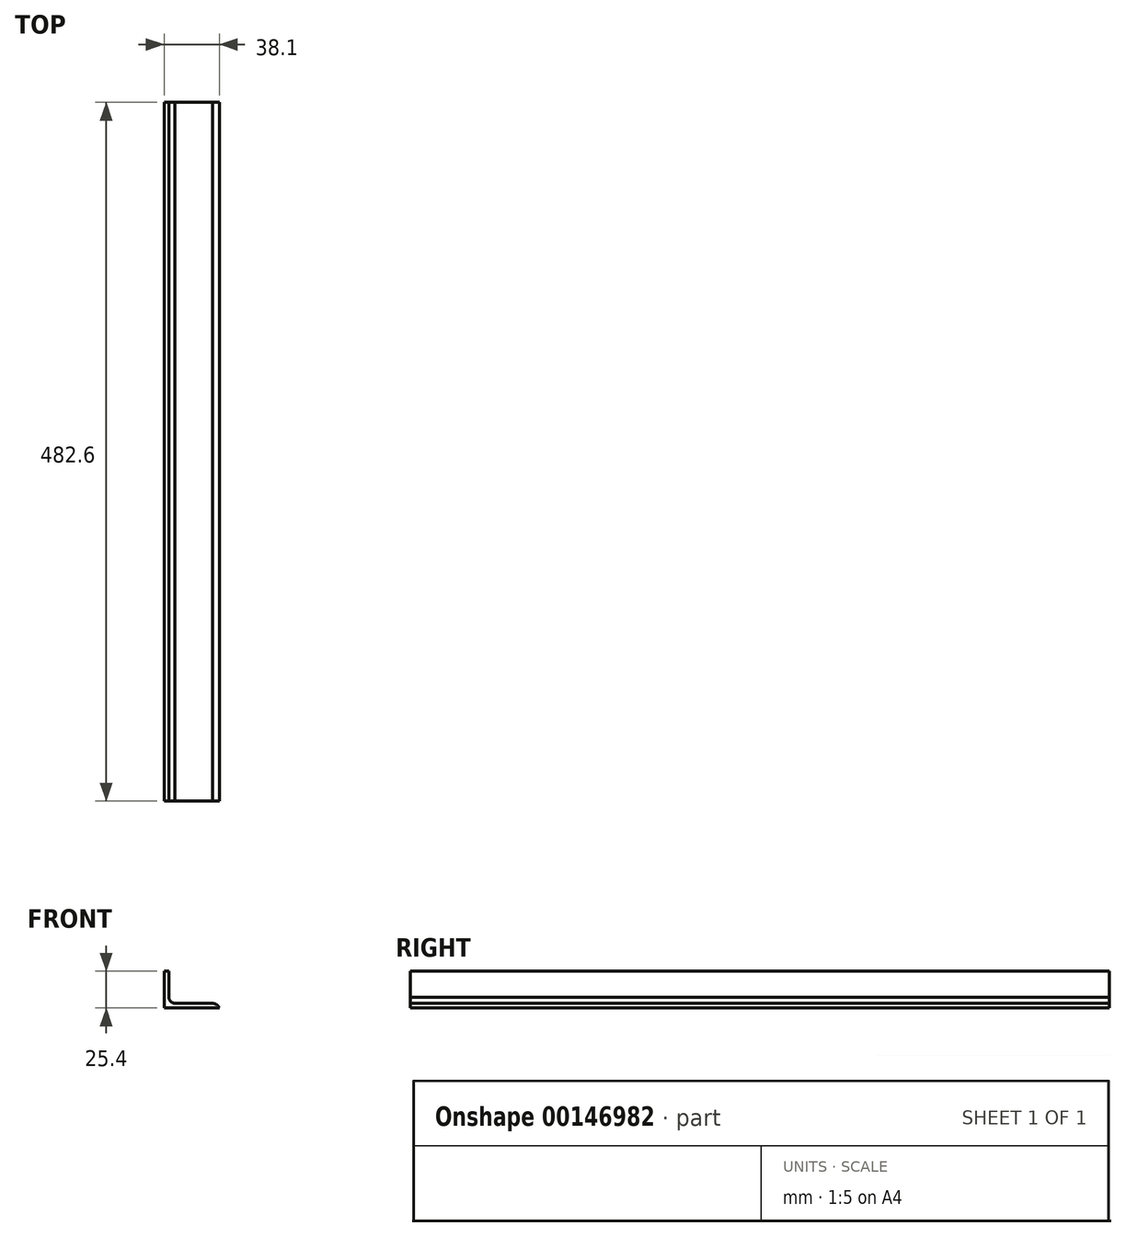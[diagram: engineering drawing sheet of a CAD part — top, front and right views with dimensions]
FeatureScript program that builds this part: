
annotation { "Feature Type Name" : "Feature", "Feature Type Description" : "" }
export const myFeature = defineFeature(function(context is Context, id is Id, definition is map)
    precondition{}
    {
        {
            var Q0;
            Q0=qCreatedBy(makeId("Front.planeOp"),FACE);
            var sketch = newSketch(context, id + "F0", { "sketchPlane" : qUnion([Q0])});
            skLineSegment(sketch, "E0.bottom", {"start": v(0, 0) * mm, "end": v(3.17, 0) * mm});
            skLineSegment(sketch, "E0.left", {"start": v(0, 0) * mm, "end": v(0, 25.4) * mm});
            skLineSegment(sketch, "E0.right", {"start": v(3.17, 7.3) * mm, "end": v(3.17, 25.4) * mm});
            skLineSegment(sketch, "E1.bottom", {"start": v(0, 0) * mm, "end": v(38.1, 0) * mm});
            skLineSegment(sketch, "E1.top", {"start": v(7.5, 3.17) * mm, "end": v(33.34, 3.17) * mm});
            skLineSegment(sketch, "E1.left", {"start": v(0, 0) * mm, "end": v(0, 3.17) * mm});
            skArc(sketch, "E2", {"start": v(38.1, 0) * mm, "mid": v(36.24, 2.37) * mm, "end": v(33.34, 3.17) * mm});
            skArc(sketch, "E3", {"start": v(3.17, 7.3) * mm, "mid": v(4.62, 4.5) * mm, "end": v(7.5, 3.17) * mm});
            skLineSegment(sketch, "E4", {"start": v(0, 25.4) * mm, "end": v(3.17, 25.4) * mm});
            skSolve(sketch);
        }
        {
            var Q0;
            Q0 = qSketchRegion(id + "F0", true);
            extrude(context, id + "F1", {"entities" : qUnion([Q0]), "depth" : 482.6 * mm});
        }
    });
